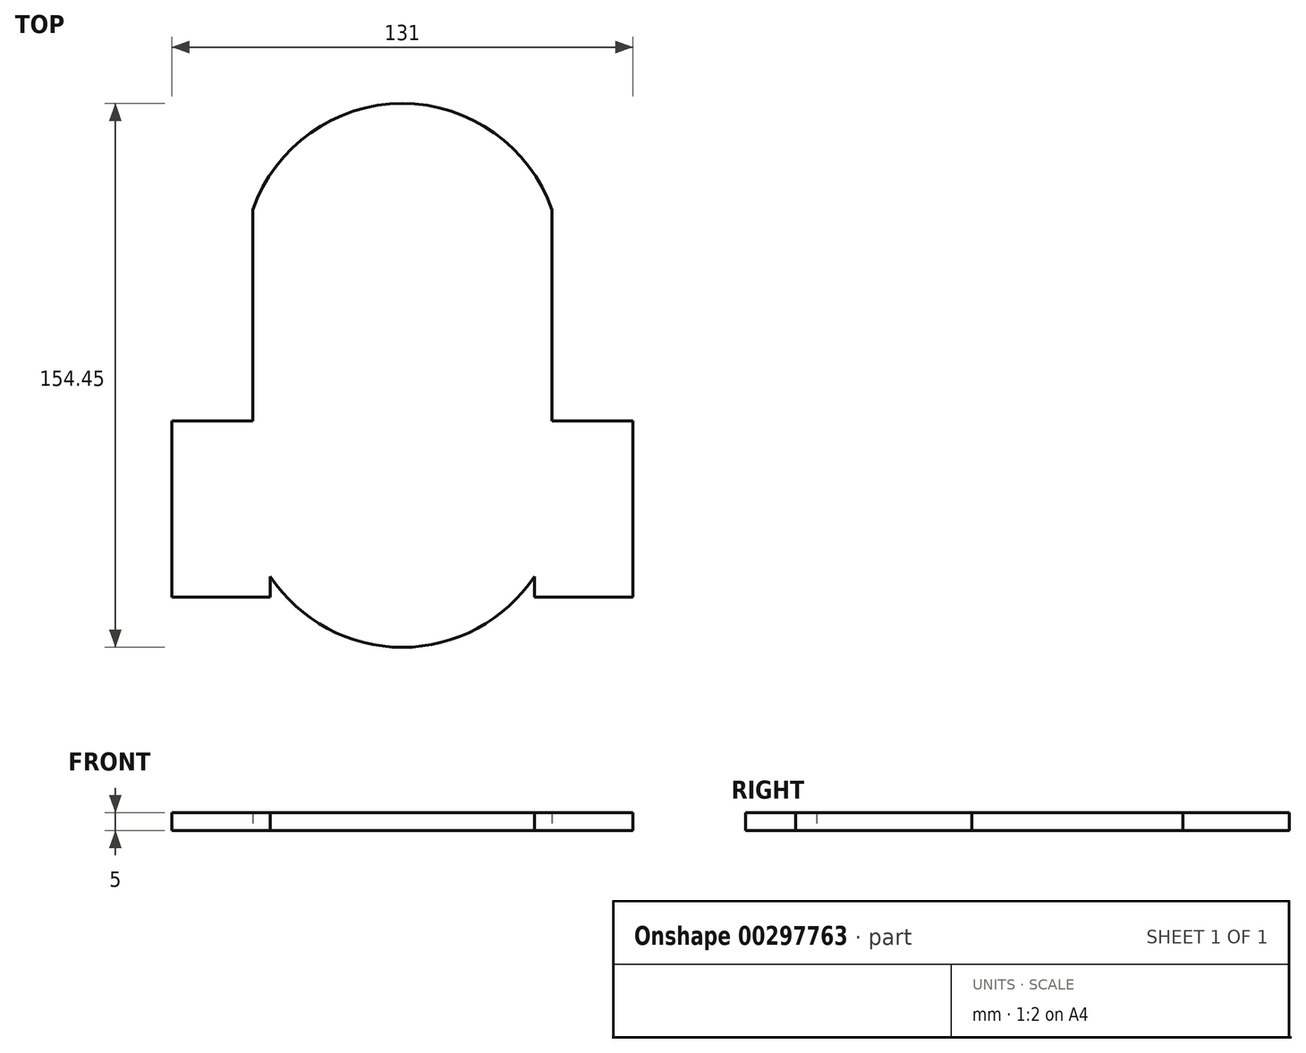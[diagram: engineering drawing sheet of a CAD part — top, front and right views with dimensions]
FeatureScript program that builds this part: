
annotation { "Feature Type Name" : "Feature", "Feature Type Description" : "" }
export const myFeature = defineFeature(function(context is Context, id is Id, definition is map)
    precondition{}
    {
        {
            var Q0;
            Q0=qCreatedBy(makeId("Top.planeOp"),FACE);
            var sketch = newSketch(context, id + "F0", { "sketchPlane" : qUnion([Q0])});
            skLineSegment(sketch, "E0.left", {"start": v(-34.26, 14.07) * mm, "end": v(-34.26, -45.93) * mm});
            skLineSegment(sketch, "E0.right", {"start": v(50.74, 14.07) * mm, "end": v(50.74, -45.93) * mm});
            skArc(sketch, "E1", {"start": v(50.74, 14.07) * mm, "mid": v(8.24, 44.28) * mm, "end": v(-34.26, 14.07) * mm});
            skLineSegment(sketch, "E2", {"start": v(-34.26, -45.93) * mm, "end": v(-57.26, -45.93) * mm});
            skLineSegment(sketch, "E3", {"start": v(50.74, -45.93) * mm, "end": v(73.74, -45.93) * mm});
            skLineSegment(sketch, "E4.top", {"start": v(-57.26, -95.93) * mm, "end": v(-29.26, -95.93) * mm});
            skLineSegment(sketch, "E4.left", {"start": v(-57.26, -45.93) * mm, "end": v(-57.26, -95.93) * mm});
            skLineSegment(sketch, "E4.right", {"start": v(-29.26, -90.05) * mm, "end": v(-29.26, -95.93) * mm});
            skLineSegment(sketch, "E5.top", {"start": v(73.74, -95.93) * mm, "end": v(45.74, -95.93) * mm});
            skLineSegment(sketch, "E5.left", {"start": v(73.74, -45.93) * mm, "end": v(73.74, -95.93) * mm});
            skLineSegment(sketch, "E5.right", {"start": v(45.74, -90.05) * mm, "end": v(45.74, -95.93) * mm});
            skArc(sketch, "E6", {"start": v(-29.26, -90.05) * mm, "mid": v(8.24, -110.17) * mm, "end": v(45.74, -90.05) * mm});
            skSolve(sketch);
        }
        {
            var Q0;
            Q0=makeQuery(id+"F0.imprint","IMPRINT",FACE,{"disambiguationData":[TD([[makeQuery(id+"F0.imprint","IMPRINT",EDGE,{"derivedFrom":sQuery(id+"F0.wireOp",EDGE,"E0.left")}),1.0]])]});
            extrude(context, id + "F1", {"entities" : qUnion([Q0]), "depth" : 5 * mm});
        }
    });
